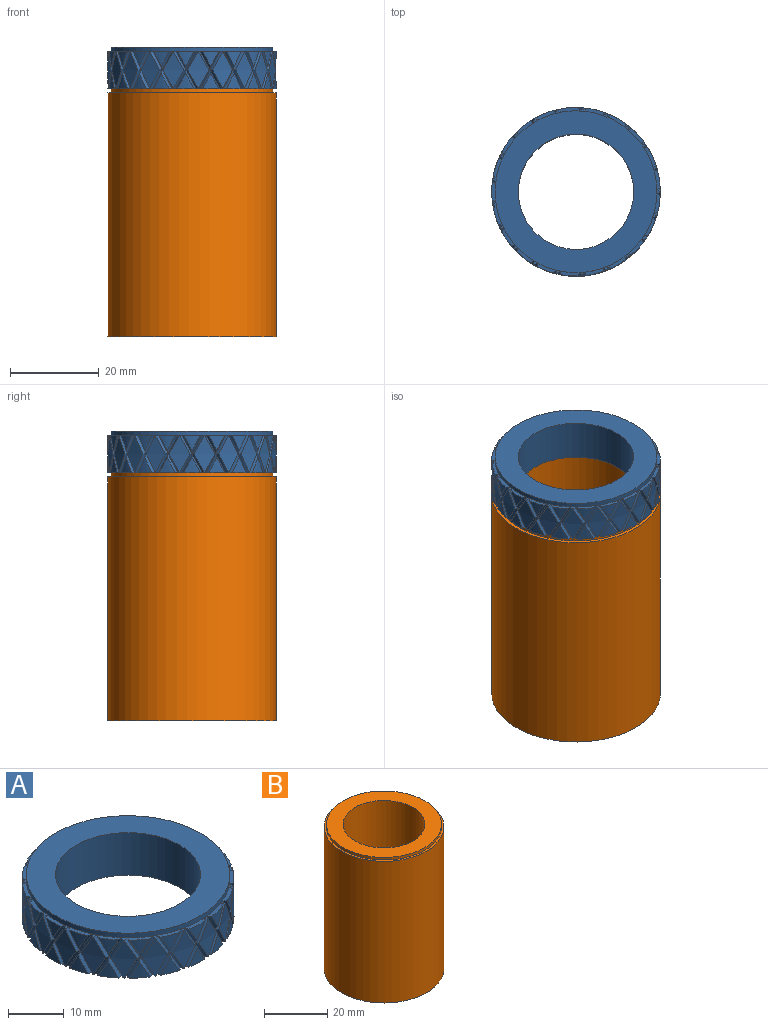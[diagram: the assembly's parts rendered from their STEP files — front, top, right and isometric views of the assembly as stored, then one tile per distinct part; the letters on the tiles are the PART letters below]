
ASSEMBLY  parts=2 mates=1
PART A: 236 faces, bbox 38.3x38.4x11.5 mm
  f0: cylinder r=19mm len=8.33mm, axis (0,0,-1), area 19.7mm2, adj f3,f7,f227,f229
  f1: cylinder r=19mm len=3.75mm, axis (0,0,-1), area 6.4mm2, adj f2,f230,f235
  f2: bspline ~11.35x5.87mm, area 3.5mm2, adj f1,f3,f230,f235
  f3: bspline ~10.27x5.98mm, area 3.9mm2, adj f0,f2,f7,f229,f235
  f4: cylinder r=19mm len=3.42mm, axis (0,0,-1), area 6.4mm2, adj f6,f228,f235
  f5: cylinder r=19mm len=3.72mm, axis (0,0,-1), area 6.2mm2, adj f106,f112,f231
  f6: bspline ~11.36x5.57mm, area 3.5mm2, adj f4,f7,f228,f235
  f7: bspline ~10.27x5.21mm, area 3.9mm2, adj f0,f3,f6,f227,f235
  f8: cylinder r=19mm len=8.33mm, axis (0,0,-1), area 19.7mm2, adj f12,f221,f223,f234
  f9: cylinder r=19mm len=3.39mm, axis (0,0,-1), area 6.2mm2, adj f106,f224,f233
  f10: cylinder r=19mm len=3.35mm, axis (0,0,-1), area 6.4mm2, adj f11,f222,f235
  f11: bspline ~5.05x2.25mm, area 3.5mm2, adj f10,f12,f222,f235
  f12: bspline ~10.27x4.47mm, area 3.9mm2, adj f8,f11,f221,f234,f235
  f13: cylinder r=19mm len=3.32mm, axis (0,0,-1), area 6.2mm2, adj f106,f218,f225
  f14: cylinder r=19mm len=8.33mm, axis (0,0,-1), area 19.7mm2, adj f17,f215,f217,f226
  f15: cylinder r=19mm len=3.35mm, axis (0,0,-1), area 6.4mm2, adj f16,f216,f235
  f16: bspline ~5.05x2.34mm, area 3.5mm2, adj f15,f17,f216,f235
  f17: bspline ~4.58x2.71mm, area 3.9mm2, adj f14,f16,f215,f226,f235
  f18: cylinder r=19mm len=3.32mm, axis (0,0,-1), area 6.2mm2, adj f106,f212,f219
  f19: cylinder r=19mm len=8.33mm, axis (0,0,-1), area 19.7mm2, adj f22,f209,f211,f220
  f20: cylinder r=19mm len=3.7mm, axis (0,0,-1), area 6.4mm2, adj f21,f210,f235
  f21: bspline ~5.05x2.44mm, area 3.5mm2, adj f20,f22,f210,f235
  f22: bspline ~10.27x5.94mm, area 3.9mm2, adj f19,f21,f209,f220,f235
  f23: cylinder r=19mm len=3.67mm, axis (0,0,-1), area 6.2mm2, adj f106,f206,f213
  f24: cylinder r=19mm len=8.33mm, axis (0,0,-1), area 19.7mm2, adj f27,f203,f205,f214
  f25: cylinder r=19mm len=3.78mm, axis (0,0,-1), area 6.4mm2, adj f26,f204,f235
  f26: bspline ~5.05x2.38mm, area 3.5mm2, adj f25,f27,f204,f235
  f27: bspline ~4.58x2.8mm, area 3.9mm2, adj f24,f26,f203,f214,f235
  f28: cylinder r=19mm len=3.75mm, axis (0,0,-1), area 6.2mm2, adj f106,f200,f207
  f29: cylinder r=19mm len=8.33mm, axis (0,0,-1), area 19.7mm2, adj f32,f197,f199,f208
  f30: cylinder r=19mm len=3.53mm, axis (0,0,-1), area 6.4mm2, adj f31,f198,f235
  f31: bspline ~5.05x2.44mm, area 3.5mm2, adj f30,f32,f198,f235
  f32: bspline ~4.58x2.47mm, area 3.9mm2, adj f29,f31,f197,f208,f235
  f33: cylinder r=19mm len=3.5mm, axis (0,0,-1), area 6.2mm2, adj f106,f194,f201
  f34: cylinder r=19mm len=8.33mm, axis (0,0,-1), area 19.7mm2, adj f37,f191,f193,f202
  f35: cylinder r=19mm len=3.35mm, axis (0,0,-1), area 6.4mm2, adj f36,f192,f235
  f36: bspline ~5.05x2.32mm, area 3.5mm2, adj f35,f37,f192,f235
  f37: bspline ~4.58x2.16mm, area 3.9mm2, adj f34,f36,f191,f202,f235
  f38: cylinder r=19mm len=3.32mm, axis (0,0,-1), area 6.2mm2, adj f106,f188,f195
  f39: cylinder r=19mm len=8.33mm, axis (0,0,-1), area 19.7mm2, adj f42,f185,f187,f196
  f40: cylinder r=19mm len=3.35mm, axis (0,0,-1), area 6.4mm2, adj f41,f186,f235
  f41: bspline ~5.05x2.28mm, area 3.5mm2, adj f40,f42,f186,f235
  f42: bspline ~10.27x5.24mm, area 3.9mm2, adj f39,f41,f185,f196,f235
  f43: cylinder r=19mm len=3.32mm, axis (0,0,-1), area 6.2mm2, adj f106,f182,f189
  f44: cylinder r=19mm len=8.33mm, axis (0,0,-1), area 19.7mm2, adj f47,f179,f181,f190
  f45: cylinder r=19mm len=3.62mm, axis (0,0,-1), area 6.4mm2, adj f46,f180,f235
  f46: bspline ~5.05x2.43mm, area 3.5mm2, adj f45,f47,f180,f235
  f47: bspline ~4.58x2.86mm, area 3.9mm2, adj f44,f46,f179,f190,f235
  f48: cylinder r=19mm len=3.59mm, axis (0,0,-1), area 6.2mm2, adj f106,f176,f183
  f49: cylinder r=19mm len=8.33mm, axis (0,0,-1), area 19.7mm2, adj f52,f173,f175,f184
  f50: cylinder r=19mm len=3.79mm, axis (0,0,-1), area 6.4mm2, adj f51,f174,f235
  f51: bspline ~5.05x2.38mm, area 3.5mm2, adj f50,f52,f174,f235
  f52: bspline ~4.58x2.84mm, area 3.9mm2, adj f49,f51,f173,f184,f235
  f53: cylinder r=19mm len=3.76mm, axis (0,0,-1), area 6.2mm2, adj f106,f170,f177
  f54: cylinder r=19mm len=8.33mm, axis (0,0,-1), area 19.7mm2, adj f57,f167,f169,f178
  f55: cylinder r=19mm len=3.62mm, axis (0,0,-1), area 6.4mm2, adj f56,f168,f235
  f56: bspline ~5.05x2.44mm, area 3.5mm2, adj f55,f57,f168,f235
  f57: bspline ~4.58x2.57mm, area 3.9mm2, adj f54,f56,f167,f178,f235
  f58: cylinder r=19mm len=3.59mm, axis (0,0,-1), area 6.2mm2, adj f106,f164,f171
  f59: cylinder r=19mm len=8.33mm, axis (0,0,-1), area 19.7mm2, adj f62,f161,f163,f172
  f60: cylinder r=19mm len=3.35mm, axis (0,0,-1), area 6.4mm2, adj f61,f162,f235
  f61: bspline ~5.05x2.37mm, area 3.5mm2, adj f60,f62,f162,f235
  f62: bspline ~10.27x4.81mm, area 3.9mm2, adj f59,f61,f161,f172,f235
  f63: cylinder r=19mm len=3.32mm, axis (0,0,-1), area 6.2mm2, adj f106,f158,f165
  f64: cylinder r=19mm len=8.33mm, axis (0,0,-1), area 19.7mm2, adj f67,f155,f157,f166
  f65: cylinder r=19mm len=3.35mm, axis (0,0,-1), area 6.4mm2, adj f66,f156,f235
  f66: bspline ~5.05x2.2mm, area 3.5mm2, adj f65,f67,f156,f235
  f67: bspline ~4.58x2.53mm, area 3.9mm2, adj f64,f66,f155,f166,f235
  f68: cylinder r=19mm len=3.32mm, axis (0,0,-1), area 6.2mm2, adj f106,f152,f159
  f69: cylinder r=19mm len=8.33mm, axis (0,0,-1), area 19.7mm2, adj f72,f149,f151,f160
  f70: cylinder r=19mm len=3.53mm, axis (0,0,-1), area 6.4mm2, adj f71,f150,f235
  f71: bspline ~5.05x2.42mm, area 3.5mm2, adj f70,f72,f150,f235
  f72: bspline ~10.27x5.76mm, area 3.9mm2, adj f69,f71,f149,f160,f235
  f73: cylinder r=19mm len=3.5mm, axis (0,0,-1), area 6.2mm2, adj f106,f146,f153
  f74: cylinder r=19mm len=8.33mm, axis (0,0,-1), area 19.7mm2, adj f77,f143,f145,f154
  f75: cylinder r=19mm len=3.78mm, axis (0,0,-1), area 6.4mm2, adj f76,f144,f235
  f76: bspline ~5.05x2.41mm, area 3.5mm2, adj f75,f77,f144,f235
  f77: bspline ~10.27x5.99mm, area 3.9mm2, adj f74,f76,f143,f154,f235
  f78: cylinder r=19mm len=3.75mm, axis (0,0,-1), area 6.2mm2, adj f106,f140,f147
  f79: cylinder r=19mm len=8.33mm, axis (0,0,-1), area 19.7mm2, adj f82,f137,f139,f148
  f80: cylinder r=19mm len=3.7mm, axis (0,0,-1), area 6.4mm2, adj f81,f138,f235
  f81: bspline ~5.05x2.42mm, area 3.5mm2, adj f80,f82,f138,f235
  f82: bspline ~10.27x5.69mm, area 3.9mm2, adj f79,f81,f137,f148,f235
  f83: cylinder r=19mm len=3.67mm, axis (0,0,-1), area 6.2mm2, adj f106,f134,f141
  f84: cylinder r=19mm len=8.33mm, axis (0,0,-1), area 19.7mm2, adj f87,f131,f133,f142
  f85: cylinder r=19mm len=3.35mm, axis (0,0,-1), area 6.4mm2, adj f86,f132,f235
  f86: bspline ~5.05x2.41mm, area 3.5mm2, adj f85,f87,f132,f235
  f87: bspline ~10.27x5.03mm, area 3.9mm2, adj f84,f86,f131,f142,f235
  f88: cylinder r=19mm len=3.32mm, axis (0,0,-1), area 6.2mm2, adj f106,f128,f135
  f89: cylinder r=19mm len=8.33mm, axis (0,0,-1), area 19.7mm2, adj f92,f125,f127,f136
  f90: cylinder r=19mm len=3.35mm, axis (0,0,-1), area 6.4mm2, adj f91,f126,f235
  f91: bspline ~5.05x2.18mm, area 3.5mm2, adj f90,f92,f126,f235
  f92: bspline ~10.27x4.75mm, area 3.9mm2, adj f89,f91,f125,f136,f235
  f93: cylinder r=19mm len=3.32mm, axis (0,0,-1), area 6.2mm2, adj f106,f122,f129
  f94: cylinder r=19mm len=8.33mm, axis (0,0,-1), area 19.7mm2, adj f97,f119,f121,f130
  f95: cylinder r=19mm len=3.42mm, axis (0,0,-1), area 6.4mm2, adj f96,f120,f235
  f96: bspline ~5.05x2.38mm, area 3.5mm2, adj f95,f97,f120,f235
  f97: bspline ~10.27x5.62mm, area 3.9mm2, adj f94,f96,f119,f130,f235
  f98: cylinder r=19mm len=3.39mm, axis (0,0,-1), area 6.2mm2, adj f106,f116,f123
  f99: cylinder r=19mm len=8.33mm, axis (0,0,-1), area 19.7mm2, adj f102,f113,f115,f124
  f100: cylinder r=19mm len=3.75mm, axis (0,0,-1), area 6.4mm2, adj f101,f114,f235
  f101: bspline ~5.05x2.43mm, area 3.5mm2, adj f100,f102,f114,f235
  f102: bspline ~10.27x5.98mm, area 3.9mm2, adj f99,f101,f113,f124,f235
  f103: cylinder r=19mm len=3.72mm, axis (0,0,-1), area 6.2mm2, adj f106,f111,f117
  f104: cylinder r=13mm len=26mm, axis (0,0,1), area 763.7mm2, adj f108,f235
  f105: cylinder r=19mm len=8.33mm, axis (0,0,-1), area 19.7mm2, adj f109,f110,f118,f232
  f106: plane 38x38mm, normal (0,0,1), area 73.8mm2, adj f5,f9,f13,f18,f23,f28,f33,f38
  f107: cylinder r=18.25mm len=36.5mm, axis (0,0,-1), area 114.7mm2, adj f106,f108
  f108: plane 36.5x36.5mm, normal (0,0,1), area 515.4mm2, adj f104,f107
  f109: bspline ~11.35x5.87mm, area 3.9mm2, adj f105,f106,f112,f232
  f110: bspline ~5.85x2.83mm, area 3.9mm2, adj f105,f106,f111,f118
  f111: bspline ~4.34x2.72mm, area 3.5mm2, adj f103,f106,f110,f117
  f112: bspline ~10.27x5.98mm, area 3.5mm2, adj f5,f106,f109,f231
  f113: bspline ~11.36x5.88mm, area 3.9mm2, adj f99,f102,f106,f117
  f114: bspline ~11.36x5.88mm, area 3.5mm2, adj f100,f101,f118,f235
  f115: bspline ~5.85x2.85mm, area 3.9mm2, adj f99,f106,f116,f124
  f116: bspline ~10.27x5.62mm, area 3.5mm2, adj f98,f106,f115,f123
  f117: bspline ~4.34x2.47mm, area 3.5mm2, adj f103,f106,f111,f113
  f118: bspline ~4.58x2.74mm, area 3.9mm2, adj f105,f110,f114,f232,f235
  f119: bspline ~11.36x5.57mm, area 3.9mm2, adj f94,f97,f106,f123
  f120: bspline ~11.36x5.57mm, area 3.5mm2, adj f95,f96,f124,f235
  f121: bspline ~5.85x2.62mm, area 3.9mm2, adj f94,f106,f122,f130
  f122: bspline ~10.27x4.75mm, area 3.5mm2, adj f93,f106,f121,f129
  f123: bspline ~4.34x2.08mm, area 3.5mm2, adj f98,f106,f116,f119
  f124: bspline ~4.58x2.35mm, area 3.9mm2, adj f99,f102,f115,f120,f235
  f125: bspline ~11.36x4.78mm, area 3.9mm2, adj f89,f92,f106,f129
  f126: bspline ~11.36x4.78mm, area 3.5mm2, adj f90,f91,f130,f235
  f127: bspline ~5.85x2.7mm, area 3.9mm2, adj f89,f106,f128,f136
  f128: bspline ~10.27x5.03mm, area 3.5mm2, adj f88,f106,f127,f135
  f129: bspline ~4.34x2.4mm, area 3.5mm2, adj f93,f106,f122,f125
  f130: bspline ~4.58x2.29mm, area 3.9mm2, adj f94,f97,f121,f126,f235
  f131: bspline ~11.36x5.38mm, area 3.9mm2, adj f84,f87,f106,f135
  f132: bspline ~11.36x5.38mm, area 3.5mm2, adj f85,f86,f136,f235
  f133: bspline ~5.85x2.87mm, area 3.9mm2, adj f84,f106,f134,f142
  f134: bspline ~4.34x2.38mm, area 3.5mm2, adj f83,f106,f133,f141
  f135: bspline ~4.34x2.7mm, area 3.5mm2, adj f88,f106,f128,f131
  f136: bspline ~4.58x2.71mm, area 3.9mm2, adj f89,f92,f127,f132,f235
  f137: bspline ~11.36x5.84mm, area 3.9mm2, adj f79,f82,f106,f141
  f138: bspline ~11.36x5.84mm, area 3.5mm2, adj f80,f81,f142,f235
  f139: bspline ~5.85x2.84mm, area 3.9mm2, adj f79,f106,f140,f148
  f140: bspline ~4.34x2.68mm, area 3.5mm2, adj f78,f106,f139,f147
  f141: bspline ~4.34x2.75mm, area 3.5mm2, adj f83,f106,f134,f137
  f142: bspline ~4.58x2.88mm, area 3.9mm2, adj f84,f87,f133,f138,f235
  f143: bspline ~11.36x5.93mm, area 3.9mm2, adj f74,f77,f106,f147
  f144: bspline ~11.36x5.93mm, area 3.5mm2, adj f75,f76,f148,f235
  f145: bspline ~5.85x2.87mm, area 3.9mm2, adj f74,f106,f146,f154
  f146: bspline ~10.27x5.76mm, area 3.5mm2, adj f73,f106,f145,f153
  f147: bspline ~4.34x2.56mm, area 3.5mm2, adj f78,f106,f140,f143
  f148: bspline ~4.58x2.8mm, area 3.9mm2, adj f79,f82,f139,f144,f235
  f149: bspline ~11.36x5.7mm, area 3.9mm2, adj f69,f72,f106,f153
  f150: bspline ~11.36x5.7mm, area 3.5mm2, adj f70,f71,f154,f235
  f151: bspline ~5.85x2.7mm, area 3.9mm2, adj f69,f106,f152,f160
  f152: bspline ~10.27x5.01mm, area 3.5mm2, adj f68,f106,f151,f159
  f153: bspline ~4.34x2.15mm, area 3.5mm2, adj f73,f106,f146,f149
  f154: bspline ~4.58x2.47mm, area 3.9mm2, adj f74,f77,f145,f150,f235
  f155: bspline ~11.36x5.02mm, area 3.9mm2, adj f64,f67,f106,f159
  f156: bspline ~11.36x5.02mm, area 3.5mm2, adj f65,f66,f160,f235
  f157: bspline ~5.85x2.62mm, area 3.9mm2, adj f64,f106,f158,f166
  f158: bspline ~10.27x4.81mm, area 3.5mm2, adj f63,f106,f157,f165
  f159: bspline ~4.34x2.29mm, area 3.5mm2, adj f68,f106,f152,f155
  f160: bspline ~4.58x2.15mm, area 3.9mm2, adj f69,f72,f151,f156,f235
  f161: bspline ~11.36x5.19mm, area 3.9mm2, adj f59,f62,f106,f165
  f162: bspline ~11.36x5.19mm, area 3.5mm2, adj f60,f61,f166,f235
  f163: bspline ~5.85x2.85mm, area 3.9mm2, adj f59,f106,f164,f172
  f164: bspline ~10.27x5.53mm, area 3.5mm2, adj f58,f106,f163,f171
  f165: bspline ~4.34x2.64mm, area 3.5mm2, adj f63,f106,f158,f161
  f166: bspline ~4.58x2.62mm, area 3.9mm2, adj f64,f67,f157,f162,f235
  f167: bspline ~11.36x5.77mm, area 3.9mm2, adj f54,f57,f106,f171
  f168: bspline ~11.36x5.77mm, area 3.5mm2, adj f55,f56,f172,f235
  f169: bspline ~5.85x2.83mm, area 3.9mm2, adj f54,f106,f170,f178
  f170: bspline ~10.27x5.96mm, area 3.5mm2, adj f53,f106,f169,f177
  f171: bspline ~4.34x2.76mm, area 3.5mm2, adj f58,f106,f164,f167
  f172: bspline ~4.58x2.86mm, area 3.9mm2, adj f59,f62,f163,f168,f235
  f173: bspline ~11.36x5.94mm, area 3.9mm2, adj f49,f52,f106,f177
  f174: bspline ~11.36x5.94mm, area 3.5mm2, adj f50,f51,f178,f235
  f175: bspline ~5.85x2.87mm, area 3.9mm2, adj f49,f106,f176,f184
  f176: bspline ~4.34x2.76mm, area 3.5mm2, adj f48,f106,f175,f183
  f177: bspline ~4.34x2.63mm, area 3.5mm2, adj f53,f106,f170,f173
  f178: bspline ~4.58x2.84mm, area 3.9mm2, adj f54,f57,f169,f174,f235
  f179: bspline ~11.36x5.79mm, area 3.9mm2, adj f44,f47,f106,f183
  f180: bspline ~11.36x5.79mm, area 3.5mm2, adj f45,f46,f184,f235
  f181: bspline ~5.85x2.76mm, area 3.9mm2, adj f44,f106,f182,f190
  f182: bspline ~4.34x2.65mm, area 3.5mm2, adj f43,f106,f181,f189
  f183: bspline ~4.34x2.26mm, area 3.5mm2, adj f48,f106,f176,f179
  f184: bspline ~4.58x2.57mm, area 3.9mm2, adj f49,f52,f175,f180,f235
  f185: bspline ~11.36x5.23mm, area 3.9mm2, adj f39,f42,f106,f189
  f186: bspline ~11.36x5.23mm, area 3.5mm2, adj f40,f41,f190,f235
  f187: bspline ~5.85x2.52mm, area 3.9mm2, adj f39,f106,f188,f196
  f188: bspline ~4.34x2.3mm, area 3.5mm2, adj f38,f106,f187,f195
  f189: bspline ~4.34x2.17mm, area 3.5mm2, adj f43,f106,f182,f185
  f190: bspline ~4.58x2.17mm, area 3.9mm2, adj f44,f47,f181,f186,f235
  f191: bspline ~11.36x4.97mm, area 3.9mm2, adj f34,f37,f106,f195
  f192: bspline ~11.36x4.97mm, area 3.5mm2, adj f35,f36,f196,f235
  f193: bspline ~5.85x2.82mm, area 3.9mm2, adj f34,f106,f194,f202
  f194: bspline ~4.34x2.15mm, area 3.5mm2, adj f33,f106,f193,f201
  f195: bspline ~4.34x2.58mm, area 3.5mm2, adj f38,f106,f188,f191
  f196: bspline ~4.58x2.53mm, area 3.9mm2, adj f39,f42,f187,f192,f235
  f197: bspline ~11.36x5.67mm, area 3.9mm2, adj f29,f32,f106,f201
  f198: bspline ~11.36x5.67mm, area 3.5mm2, adj f30,f31,f202,f235
  f199: bspline ~5.85x2.86mm, area 3.9mm2, adj f29,f106,f200,f208
  f200: bspline ~4.34x2.56mm, area 3.5mm2, adj f28,f106,f199,f207
  f201: bspline ~4.34x2.75mm, area 3.5mm2, adj f33,f106,f194,f197
  f202: bspline ~4.58x2.82mm, area 3.9mm2, adj f34,f37,f193,f198,f235
  f203: bspline ~11.36x5.92mm, area 3.9mm2, adj f24,f27,f106,f207
  f204: bspline ~11.36x5.92mm, area 3.5mm2, adj f25,f26,f208,f235
  f205: bspline ~5.85x2.86mm, area 3.9mm2, adj f24,f106,f206,f214
  f206: bspline ~10.27x5.94mm, area 3.5mm2, adj f23,f106,f205,f213
  f207: bspline ~4.34x2.68mm, area 3.5mm2, adj f28,f106,f200,f203
  f208: bspline ~4.58x2.87mm, area 3.9mm2, adj f29,f32,f199,f204,f235
  f209: bspline ~11.36x5.85mm, area 3.9mm2, adj f19,f22,f106,f213
  f210: bspline ~11.36x5.85mm, area 3.5mm2, adj f20,f21,f214,f235
  f211: bspline ~5.85x2.82mm, area 3.9mm2, adj f19,f106,f212,f220
  f212: bspline ~4.34x2.7mm, area 3.5mm2, adj f18,f106,f211,f219
  f213: bspline ~4.34x2.38mm, area 3.5mm2, adj f23,f106,f206,f209
  f214: bspline ~4.58x2.66mm, area 3.9mm2, adj f24,f27,f205,f210,f235
  f215: bspline ~11.36x5.42mm, area 3.9mm2, adj f14,f17,f106,f219
  f216: bspline ~11.36x5.42mm, area 3.5mm2, adj f15,f16,f220,f235
  f217: bspline ~5.85x2.52mm, area 3.9mm2, adj f14,f106,f218,f226
  f218: bspline ~4.34x2.4mm, area 3.5mm2, adj f13,f106,f217,f225
  f219: bspline ~4.34x2.04mm, area 3.5mm2, adj f18,f106,f212,f215
  f220: bspline ~4.58x2.25mm, area 3.9mm2, adj f19,f22,f211,f216,f235
  f221: bspline ~11.36x4.73mm, area 3.9mm2, adj f8,f12,f106,f225
  f222: bspline ~11.36x4.73mm, area 3.5mm2, adj f10,f11,f226,f235
  f223: bspline ~11.36x5.57mm, area 3.9mm2, adj f8,f106,f224,f234
  f224: bspline ~10.27x5.21mm, area 3.5mm2, adj f9,f106,f223,f233
  f225: bspline ~4.34x2.5mm, area 3.5mm2, adj f13,f106,f218,f221
  f226: bspline ~4.58x2.42mm, area 3.9mm2, adj f14,f17,f217,f222,f235
  f227: bspline ~11.36x5.55mm, area 3.9mm2, adj f0,f7,f106,f233
  f228: bspline ~11.36x5.55mm, area 3.5mm2, adj f4,f6,f234,f235
  f229: bspline ~11.36x5.88mm, area 3.9mm2, adj f0,f3,f106,f231
  f230: bspline ~11.36x5.88mm, area 3.5mm2, adj f1,f2,f232,f235
  f231: bspline ~4.34x2.47mm, area 3.5mm2, adj f5,f106,f112,f229
  f232: bspline ~4.58x2.74mm, area 3.9mm2, adj f105,f109,f118,f230,f235
  f233: bspline ~4.34x2.73mm, area 3.5mm2, adj f9,f106,f224,f227
  f234: bspline ~4.58x2.77mm, area 3.9mm2, adj f8,f12,f223,f228,f235
  f235: plane 38x37.98mm, normal (0,0,-1), area 589.1mm2, adj f1,f2,f3,f4,f6,f7,f10,f11
PART B: 6 faces, bbox 38x38x56 mm
  f0: cylinder r=13mm len=56mm, axis (0,0,-1), area 4574.2mm2, adj f3,f5
  f1: cylinder r=19mm len=55mm, axis (0,0,-1), area 6565.9mm2, adj f2,f3
  f2: plane 38x38mm, normal (0,0,1), area 87.8mm2, adj f1,f4
  f3: plane 38x38mm, normal (0,0,-1), area 603.2mm2, adj f0,f1
  f4: cylinder r=18.25mm len=36.5mm, axis (0,0,-1), area 114.7mm2, adj f2,f5
  f5: plane 36.5x36.5mm, normal (0,0,1), area 515.4mm2, adj f0,f4
PLACE A t=(-47.58,-5.78,-83.33)mm
PLACE B t=(-47.58,-5.78,-27.68)mm
MATE fastened B.f4 <-> A.f107  axis (0,0,1) through (-47.58,-5.78,28.32)mm
